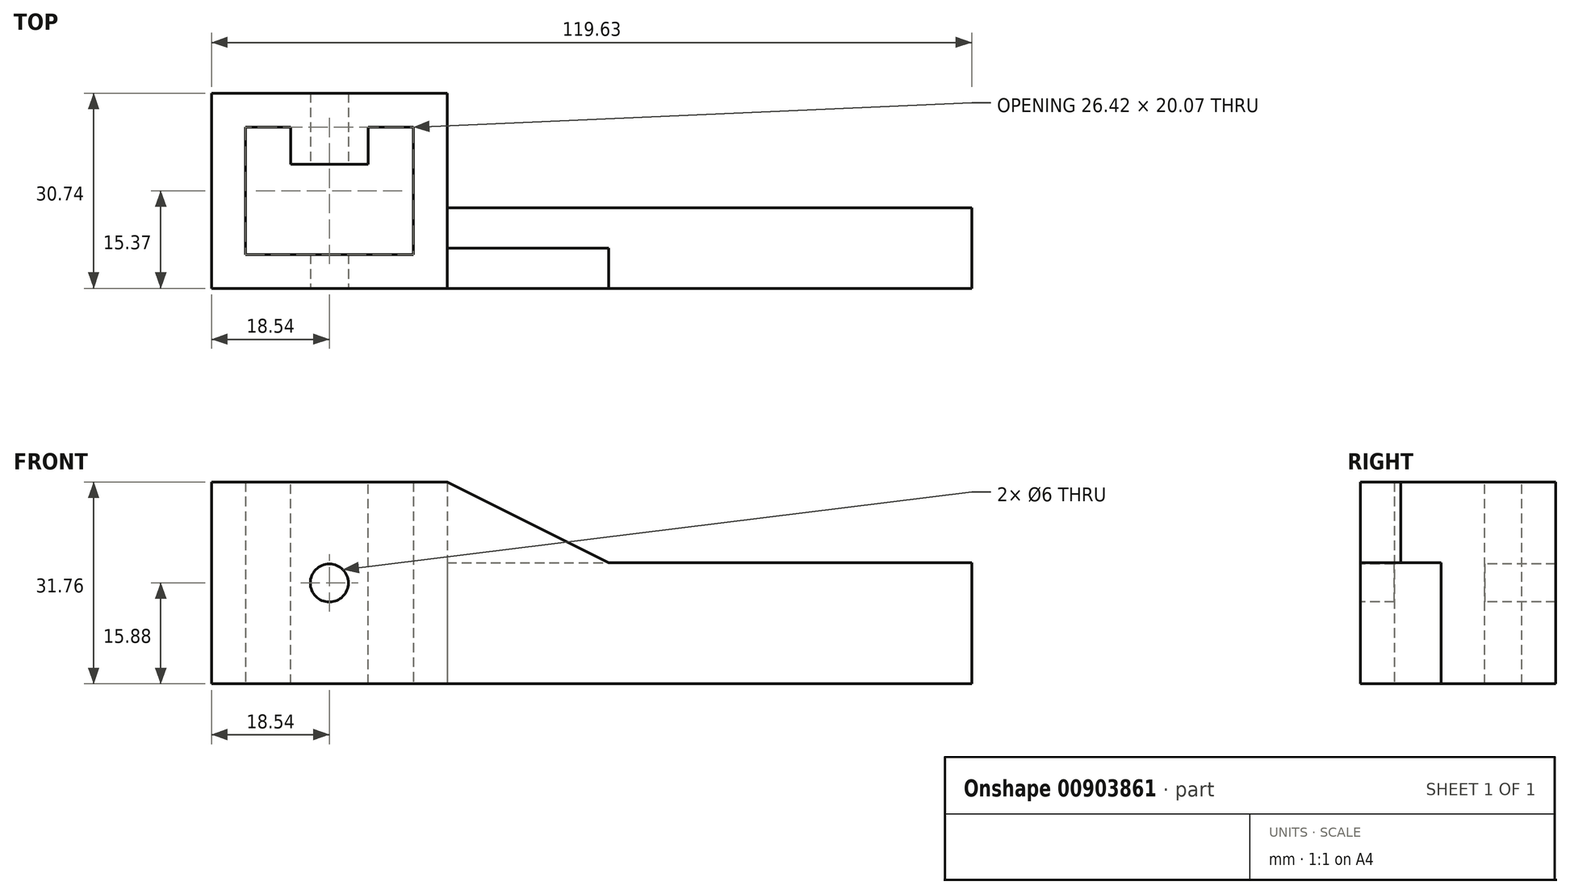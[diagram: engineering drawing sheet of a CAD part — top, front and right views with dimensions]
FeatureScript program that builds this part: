
annotation { "Feature Type Name" : "Feature", "Feature Type Description" : "" }
export const myFeature = defineFeature(function(context is Context, id is Id, definition is map)
    precondition{}
    {
        {
            var Q0;
            Q0=qCreatedBy(makeId("Top.planeOp"),FACE);
            var sketch = newSketch(context, id + "F0", { "sketchPlane" : qUnion([Q0])});
            skLineSegment(sketch, "E0.bottom", {"start": v(13.2, -10.03) * mm, "end": v(-13.2, -10.03) * mm});
            skLineSegment(sketch, "E0.top", {"start": v(13.2, 10.03) * mm, "end": v(-13.2, 10.03) * mm});
            skLineSegment(sketch, "E0.left", {"start": v(13.2, -10.03) * mm, "end": v(13.2, 10.03) * mm});
            skLineSegment(sketch, "E0.right", {"start": v(-13.2, -10.03) * mm, "end": v(-13.2, 10.03) * mm});
            skPoint(sketch, "E0.middle", {"position": v(0, 0) * mm});
            skLineSegment(sketch, "E1.0", {"start": v(-18.54, -15.37) * mm, "end": v(-18.54, 15.37) * mm});
            skLineSegment(sketch, "E1.1", {"start": v(18.54, -15.37) * mm, "end": v(-18.54, -15.37) * mm});
            skLineSegment(sketch, "E1.2", {"start": v(18.54, -15.37) * mm, "end": v(18.54, 15.37) * mm});
            skLineSegment(sketch, "E1.3", {"start": v(18.54, 15.37) * mm, "end": v(-18.54, 15.37) * mm});
            skSolve(sketch);
        }
        {
            var Q0;
            Q0=makeQuery(id+"F0.imprint","IMPRINT",FACE,{"disambiguationData":[TD([[makeQuery(id+"F0.imprint","IMPRINT",EDGE,{"derivedFrom":sQuery(id+"F0.wireOp",EDGE,"E0.bottom")}),1.0]])]});
            extrude(context, id + "F1", {"entities" : qUnion([Q0]), "endBound" : BoundingType.SYMMETRIC, "depth" : 31.75 * mm, "offsetDistance" : 25.4 * mm});
        }
        {
            var Q0;
            Q0=makeQuery(id+"F1.opExtrude","CAP_FACE",FACE,{"disambiguationData":[OSD([sQuery(id+"F0.wireOp",EDGE,"E0.bottom"),sQuery(id+"F0.wireOp",EDGE,"E0.top"),sQuery(id+"F0.wireOp",EDGE,"E0.left"),sQuery(id+"F0.wireOp",EDGE,"E0.right"),sQuery(id+"F0.wireOp",EDGE,"E1.0"),sQuery(id+"F0.wireOp",EDGE,"E1.1"),sQuery(id+"F0.wireOp",EDGE,"E1.2"),sQuery(id+"F0.wireOp",EDGE,"E1.3")])],"isStart":false});
            var sketch = newSketch(context, id + "F2", { "sketchPlane" : qUnion([Q0])});
            skLineSegment(sketch, "E2.bottom", {"start": v(6.1, 10.03) * mm, "end": v(-6.1, 10.03) * mm});
            skLineSegment(sketch, "E2.top", {"start": v(6.1, 4.2) * mm, "end": v(-6.1, 4.2) * mm});
            skLineSegment(sketch, "E2.left", {"start": v(6.1, 10.03) * mm, "end": v(6.1, 4.2) * mm});
            skLineSegment(sketch, "E2.right", {"start": v(-6.1, 10.03) * mm, "end": v(-6.1, 4.2) * mm});
            skPoint(sketch, "E2.middle", {"position": v(0, 7.11) * mm});
            skPoint(sketch, "E2.middle.positionSnap0", {"position": v(0, 10.03) * mm});
            skPoint(sketch, "E2.centerSnap0", {"position": v(0, 10.03) * mm});
            skSolve(sketch);
        }
        {
            var Q0;
            Q0=makeQuery(id+"F2.imprint","IMPRINT",FACE,{"disambiguationData":[TD([[makeQuery(id+"F2.imprint","IMPRINT",EDGE,{"derivedFrom":sQuery(id+"F2.wireOp",EDGE,"E2.bottom")}),1.0]])]});
            extrude(context, id + "F3", {"entities" : qUnion([Q0]), "operationType" : NewBodyOperationType.ADD, "oppositeDirection" : true, "depth" : 31.75 * mm, "offsetDistance" : 25.4 * mm});
        }
        {
            var Q0;
            Q0=makeQuery(id+"F3.boolean.opBoolean","MERGE",FACE,{"derivedFrom":[makeQuery(id+"F1.opExtrude","CAP_FACE",FACE,{"disambiguationData":[OSD([sQuery(id+"F0.wireOp",EDGE,"E0.bottom"),sQuery(id+"F0.wireOp",EDGE,"E0.top"),sQuery(id+"F0.wireOp",EDGE,"E0.left"),sQuery(id+"F0.wireOp",EDGE,"E0.right"),sQuery(id+"F0.wireOp",EDGE,"E1.0"),sQuery(id+"F0.wireOp",EDGE,"E1.1"),sQuery(id+"F0.wireOp",EDGE,"E1.2"),sQuery(id+"F0.wireOp",EDGE,"E1.3")])],"isStart":true}),makeQuery(id+"F3.opExtrude","CAP_FACE",FACE,{"disambiguationData":[OSD([sQuery(id+"F2.wireOp",EDGE,"E2.bottom"),sQuery(id+"F2.wireOp",EDGE,"E2.top"),sQuery(id+"F2.wireOp",EDGE,"E2.left"),sQuery(id+"F2.wireOp",EDGE,"E2.right")])],"isStart":false})]});
            var sketch = newSketch(context, id + "F4", { "sketchPlane" : qUnion([Q0])});
            skLineSegment(sketch, "E3.bottom", {"start": v(18.54, 15.37) * mm, "end": v(101.1, 15.37) * mm});
            skLineSegment(sketch, "E3.top", {"start": v(18.54, 2.67) * mm, "end": v(101.1, 2.67) * mm});
            skLineSegment(sketch, "E3.left", {"start": v(18.54, 15.37) * mm, "end": v(18.54, 2.67) * mm});
            skLineSegment(sketch, "E3.right", {"start": v(101.1, 15.37) * mm, "end": v(101.1, 2.67) * mm});
            skSolve(sketch);
        }
        {
            var Q0;
            Q0=makeQuery(id+"F4.imprint","IMPRINT",FACE,{"disambiguationData":[TD([[makeQuery(id+"F4.imprint","IMPRINT",EDGE,{"derivedFrom":sQuery(id+"F4.wireOp",EDGE,"E3.bottom")}),-1.0]])]});
            extrude(context, id + "F5", {"entities" : qUnion([Q0]), "operationType" : NewBodyOperationType.ADD, "oppositeDirection" : true, "depth" : 19.05 * mm, "offsetDistance" : 25.4 * mm});
        }
        {
            var Q0;
            Q0=makeQuery(id+"F5.boolean.opBoolean","MERGE",FACE,{"derivedFrom":[makeQuery(id+"F1.opExtrude","SWEPT_FACE",FACE,{"disambiguationData":[OSD([sQuery(id+"F0.wireOp",EDGE,"E1.1")])]}),makeQuery(id+"F5.opExtrude","SWEPT_FACE",FACE,{"disambiguationData":[OSD([sQuery(id+"F4.wireOp",EDGE,"E3.bottom")])]})]});
            var sketch = newSketch(context, id + "F6", { "sketchPlane" : qUnion([Q0])});
            skLineSegment(sketch, "E4", {"start": v(18.54, 15.88) * mm, "end": v(18.54, 3.18) * mm});
            skLineSegment(sketch, "E5", {"start": v(18.54, 3.18) * mm, "end": v(43.94, 3.18) * mm});
            skLineSegment(sketch, "E6", {"start": v(18.54, 15.88) * mm, "end": v(43.94, 3.18) * mm});
            skSolve(sketch);
        }
        {
            var Q0;
            Q0 = qSketchRegion(id + "F6", true);
            extrude(context, id + "F7", {"entities" : qUnion([Q0]), "operationType" : NewBodyOperationType.ADD, "oppositeDirection" : true, "depth" : 6.35 * mm, "offsetDistance" : 25.4 * mm});
        }
        {
            var Q0;
            Q0=makeQuery(id+"F7.boolean.opBoolean","MERGE",FACE,{"derivedFrom":[makeQuery(id+"F5.boolean.opBoolean","MERGE",FACE,{"derivedFrom":[makeQuery(id+"F1.opExtrude","SWEPT_FACE",FACE,{"disambiguationData":[OSD([sQuery(id+"F0.wireOp",EDGE,"E1.1")])]}),makeQuery(id+"F5.opExtrude","SWEPT_FACE",FACE,{"disambiguationData":[OSD([sQuery(id+"F4.wireOp",EDGE,"E3.bottom")])]})]}),makeQuery(id+"F7.opExtrude","CAP_FACE",FACE,{"disambiguationData":[OSD([sQuery(id+"F6.wireOp",EDGE,"E4"),sQuery(id+"F6.wireOp",EDGE,"E5"),sQuery(id+"F6.wireOp",EDGE,"E6")])],"isStart":true})]});
            var sketch = newSketch(context, id + "F8", { "sketchPlane" : qUnion([Q0])});
            skSolve(sketch);
        }
        {
            var Q0;
            {var subQ1=sQuery(id+"F0.wireOp",EDGE,"E1.1");Q0=makeQuery(id+"F8.imprint","IMPRINT",FACE,{"disambiguationData":[TD([[makeQuery(id+"F8.imprint","IMPRINT",EDGE,{"derivedFrom":makeQuery(id+"F1.opExtrude","CAP_EDGE",EDGE,{"disambiguationData":[OSD([subQ1])],"isStart":false})}),1.0]])]});}
            var sketch = newSketch(context, id + "F9", { "sketchPlane" : qUnion([Q0])});
            skCircle(sketch, "E7", {"center": v(0, 0) * mm, "radius": 3 * mm});
            skSolve(sketch);
        }
        {
            var Q0;
            Q0 = qSketchRegion(id + "F9", true);
            extrude(context, id + "F10", {"entities" : qUnion([Q0]), "operationType" : NewBodyOperationType.REMOVE, "endBound" : BoundingType.THROUGH_ALL, "oppositeDirection" : true, "depth" : 25.4 * mm, "offsetDistance" : 25.4 * mm});
        }
    });
